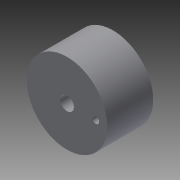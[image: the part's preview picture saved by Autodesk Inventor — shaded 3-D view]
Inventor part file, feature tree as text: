
AUTODESK INVENTOR PART (.ipt)
format: ipt  version: 2015 (Build 190159000, 159)  size: 93,696 bytes
history: native  units: mm
features: extrude x4, sketch x4
ambient origin geometry x8: Origin, YZ Plane, XZ Plane, XY Plane, X Axis, Y Axis, Z Axis, Center Point
bodies: Solid1 (feature_tree)
feature tree (8):
  extrude  "Extrusion1"  Depth=40.0mm
  extrude  "Extrusion2"  Depth=10.0mm
  extrude  "Extrusion3"  Depth=40.0mm TaperAngle=0.0deg
  extrude  "Extrusion4"  [1 undecoded]
  sketch  "Sketch1"  dims[d2=40.0mm d3=0.0mm d4=31.0mm]
  sketch  "Sketch2"  dims[d5=10.0mm d6=0.0mm d7=12.0mm]
  sketch  "Sketch3"  dims[d8=40.0mm d9=0.0mm d12=40.0mm d13=0.0mm]
  sketch  "Sketch4"  dims[d14=6.0mm]
note: 1 required parameter value undecoded (feature->parameter linkage not recoverable at this tier; creation-order binding heuristic only, values carry confidence <= 0.55)
